# Revit family: ewf_ewg_ewh_ewj-20_105a_b_y_sa2_ta(40a)2-(-50)_50Hz
name_source: partatom
category: 機械設備
units: mm (PartAtom-declared; Revit-internal decimal feet)

## family parameters
OmniClass タイトル = Industrial Ventilating Equipment
OmniClass 番号 = 23.75.35.21.17
パーツ タイプ = 標準
ロード時にボイドで切り取り = はい
丸型コネクタ寸法 = 直径を使用
作業面ベース = いいえ
共有 = いいえ
常に垂直 = はい
部屋計算ポイント = はい

## types (71) — shared parameters
IfcExportAs = IfcFanType
IfcExportType = TUBEAXIAL
MID風量 = 0.0 m³/h
MIN風量 = 0.0 m³/h
OmniClassCode = 23-33 31 19 11 17
URL = https://www.mitsubishielectric.co.jp
Uniclass2015Code = Pr_65_67_29_67
Uniclass2015Title = Propeller fans
Uniclass2015Version = Systems v1.9
ファンの種類 = 軸流羽根
仕様書バージョン = Version1.0
企業コード = 108420
分類コード = 50052503100110
周波数 = 50 Hz
呼称 = 有圧扇
法定耐用年数 = 15
製品リリース年月 = 2022年6月
製品出荷対象 = 国内
製造元 = 三菱電機株式会社
設置方法 = 壁付
説明 = 産業用有圧換気扇 低騒音形 給気専用
負荷分類 = 3_ファン類
運転質量 = 0.00 kg

## per-type parameters (varying)
- EWF-20YSA2-Q: Depth=197; Height=320; MAX風量=660.0 m³/h; Width=320; オリフィス_Depth=100  [stored 0.328084 ft]; オリフィス径=233  [stored 0.764436 ft]; フレームの厚さ=10  [stored 0.0328084 ft]; モデル=EWF-20YSA2-Q; モーター径=5  [stored 0.0164042 ft]; モーター表示=いいえ; レグ_Depth=182  [stored 0.597113 ft]; レグ_Height=230  [stored 0.754593 ft]; レグ_Width=230  [stored 0.754593 ft]; 価格=45400 $; 極=4; 極数=2; 消費電力=30 W; 相=1; 羽根径=∅200; 製品質量=3.30 kg; 質量=3.96 kg; 銘板_H=52; 銘板_Height=136; 銘板_Width=103; 銘板表示=はい; 電動機出力=15 W; 電圧=100 V
- EWF-25ASA2-Q: Depth=201  [stored 0.659449 ft]; Height=370; MAX風量=1140.0 m³/h; Width=370; オリフィス_Depth=110  [stored 0.360892 ft]; オリフィス径=283; フレームの厚さ=10  [stored 0.0328084 ft]; モデル=EWF-25ASA2-Q; モーター径=5  [stored 0.0164042 ft]; モーター表示=いいえ; レグ_Depth=182  [stored 0.597113 ft]; レグ_Height=280; レグ_Width=280; 価格=48100 $; 極=4; 極数=2; 消費電力=42 W; 相=1; 羽根径=∅250; 製品質量=4.30 kg; 質量=5.16 kg; 銘板_H=60  [stored 0.19685 ft]; 銘板_Height=153  [stored 0.501969 ft]; 銘板_Width=120  [stored 0.393701 ft]; 銘板表示=はい; 電動機出力=25 W; 電圧=100 V
- EWF-30BSA2-Q: Depth=197; Height=420; MAX風量=1680.0 m³/h; Width=420; オリフィス_Depth=110  [stored 0.360892 ft]; オリフィス径=323; フレームの厚さ=10  [stored 0.0328084 ft]; モデル=EWF-30BSA2-Q; モーター径=5  [stored 0.0164042 ft]; モーター表示=いいえ; レグ_Depth=179  [stored 0.58727 ft]; レグ_Height=330; レグ_Width=330; 価格=62000 $; 極=4; 極数=2; 消費電力=73 W; 相=1; 羽根径=∅300; 製品質量=5.80 kg; 質量=6.96 kg; 銘板_H=60  [stored 0.19685 ft]; 銘板_Height=153  [stored 0.501969 ft]; 銘板_Width=120  [stored 0.393701 ft]; 銘板表示=はい; 電動機出力=50 W; 電圧=100 V
- EWF-35CSA2-Q: Depth=208; Height=470; MAX風量=2400.0 m³/h; Width=470; オリフィス_Depth=130  [stored 0.426509 ft]; オリフィス径=373; フレームの厚さ=10  [stored 0.0328084 ft]; モデル=EWF-35CSA2-Q; モーター径=5  [stored 0.0164042 ft]; モーター表示=いいえ; レグ_Depth=190; レグ_Height=385; レグ_Width=385; 価格=82500 $; 極=4; 極数=2; 消費電力=91 W; 相=1; 羽根径=∅350; 製品質量=6.60 kg; 質量=7.92 kg; 銘板_H=60  [stored 0.19685 ft]; 銘板_Height=153  [stored 0.501969 ft]; 銘板_Width=120  [stored 0.393701 ft]; 銘板表示=はい; 電動機出力=100 W; 電圧=100 V
- EWF-35DSA2-Q: Depth=259; Height=470; MAX風量=3000.0 m³/h; Width=470; オリフィス_Depth=130  [stored 0.426509 ft]; オリフィス径=373; フレームの厚さ=10  [stored 0.0328084 ft]; モデル=EWF-35DSA2-Q; モーター径=5  [stored 0.0164042 ft]; モーター表示=いいえ; レグ_Depth=227; レグ_Height=385; レグ_Width=385; 価格=90800 $; 極=4; 極数=2; 消費電力=129 W; 相=1; 羽根径=∅350; 製品質量=9.50 kg; 質量=11.40 kg; 銘板_H=73  [stored 0.239501 ft]; 銘板_Height=181  [stored 0.593832 ft]; 銘板_Width=148  [stored 0.485564 ft]; 銘板表示=はい; 電動機出力=150 W; 電圧=100 V
- EWF-40DSA2-Q: Depth=266; Height=520; MAX風量=3720.0 m³/h; Width=520; オリフィス_Depth=135  [stored 0.442913 ft]; オリフィス径=423; フレームの厚さ=10  [stored 0.0328084 ft]; モデル=EWF-40DSA2-Q; モーター径=5  [stored 0.0164042 ft]; モーター表示=いいえ; レグ_Depth=237; レグ_Height=413; レグ_Width=413; 価格=107000 $; 極=4; 極数=2; 消費電力=152 W; 相=1; 羽根径=∅400; 製品質量=12.10 kg; 質量=14.52 kg; 銘板_H=73  [stored 0.239501 ft]; 銘板_Height=181  [stored 0.593832 ft]; 銘板_Width=148  [stored 0.485564 ft]; 銘板表示=はい; 電動機出力=200 W; 電圧=100 V
- EWG-40BSA2-Q: Depth=223  [stored 0.731627 ft]; Height=520; MAX風量=2340.0 m³/h; Width=520; オリフィス_Depth=135  [stored 0.442913 ft]; オリフィス径=423; フレームの厚さ=10  [stored 0.0328084 ft]; モデル=EWG-40BSA2-Q; モーター径=5  [stored 0.0164042 ft]; モーター表示=いいえ; レグ_Depth=207  [stored 0.679134 ft]; レグ_Height=413; レグ_Width=413; 価格=89400 $; 極=6; 極数=2; 消費電力=62 W; 相=1; 羽根径=∅400; 製品質量=8.40 kg; 質量=10.08 kg; 銘板_H=60  [stored 0.19685 ft]; 銘板_Height=153  [stored 0.501969 ft]; 銘板_Width=120  [stored 0.393701 ft]; 銘板表示=はい; 電動機出力=50 W; 電圧=100 V
- EWG-40CSA2-Q: Depth=285; Height=520; MAX風量=3180.0 m³/h; Width=520; オリフィス_Depth=135  [stored 0.442913 ft]; オリフィス径=423; フレームの厚さ=10  [stored 0.0328084 ft]; モデル=EWG-40CSA2-Q; モーター径=5  [stored 0.0164042 ft]; モーター表示=いいえ; レグ_Depth=256; レグ_Height=413; レグ_Width=413; 価格=105000 $; 極=6; 極数=2; 消費電力=112 W; 相=1; 羽根径=∅400; 製品質量=12.20 kg; 質量=14.64 kg; 銘板_H=73  [stored 0.239501 ft]; 銘板_Height=181  [stored 0.593832 ft]; 銘板_Width=148  [stored 0.485564 ft]; 銘板表示=はい; 電動機出力=100 W; 電圧=100 V
- EWF-45ESA2-Q: Depth=307; Height=620; MAX風量=5560.0 m³/h; Width=620; オリフィス_Depth=135  [stored 0.442913 ft]; オリフィス径=473; フレームの厚さ=10  [stored 0.0328084 ft]; モデル=EWF-45ESA2-Q; モーター径=5  [stored 0.0164042 ft]; モーター表示=いいえ; レグ_Depth=274; レグ_Height=522; レグ_Width=522; 価格=135000 $; 極=4; 極数=2; 消費電力=262 W; 相=1; 羽根径=∅450; 製品質量=18.30 kg; 質量=21.96 kg; 銘板_H=88  [stored 0.288714 ft]; 銘板_Height=211  [stored 0.692257 ft]; 銘板_Width=178  [stored 0.58399 ft]; 銘板表示=はい; 電動機出力=400 W; 電圧=100 V
- EWG-45DSA2-Q: Depth=335; Height=620; MAX風量=4200.0 m³/h; Width=620; オリフィス_Depth=135  [stored 0.442913 ft]; オリフィス径=473; フレームの厚さ=10  [stored 0.0328084 ft]; モデル=EWG-45DSA2-Q; モーター径=5  [stored 0.0164042 ft]; モーター表示=いいえ; レグ_Depth=302; レグ_Height=514; レグ_Width=514; 価格=123000 $; 極=6; 極数=2; 消費電力=175 W; 相=1; 羽根径=∅450; 製品質量=16.90 kg; 質量=20.28 kg; 銘板_H=88  [stored 0.288714 ft]; 銘板_Height=211  [stored 0.692257 ft]; 銘板_Width=178  [stored 0.58399 ft]; 銘板表示=はい; 電動機出力=200 W; 電圧=100 V
- EWF-25ATA2-Q_200V: Depth=211  [stored 0.692257 ft]; Height=370; MAX風量=1140.0 m³/h; Width=370; オリフィス_Depth=110  [stored 0.360892 ft]; オリフィス径=283; フレームの厚さ=10  [stored 0.0328084 ft]; モデル=EWF-25ATA2-Q; モーター径=5  [stored 0.0164042 ft]; モーター表示=いいえ; レグ_Depth=197; レグ_Height=280; レグ_Width=280; 価格=48100 $; 極=4; 極数=3; 消費電力=35 W; 相=3; 羽根径=∅250; 製品質量=4.90 kg; 質量=5.88 kg; 銘板_H=60  [stored 0.19685 ft]; 銘板_Height=153  [stored 0.501969 ft]; 銘板_Width=120  [stored 0.393701 ft]; 銘板表示=はい; 電動機出力=25 W; 電圧=200 V
- EWF-30BTA2-Q_200V: Depth=197; Height=420; MAX風量=1680.0 m³/h; Width=420; オリフィス_Depth=110  [stored 0.360892 ft]; オリフィス径=323; フレームの厚さ=10  [stored 0.0328084 ft]; モデル=EWF-30BTA2-Q; モーター径=5  [stored 0.0164042 ft]; モーター表示=いいえ; レグ_Depth=179  [stored 0.58727 ft]; レグ_Height=330; レグ_Width=330; 価格=62000 $; 極=4; 極数=3; 消費電力=57 W; 相=3; 羽根径=∅300; 製品質量=5.80 kg; 質量=6.96 kg; 銘板_H=60  [stored 0.19685 ft]; 銘板_Height=153  [stored 0.501969 ft]; 銘板_Width=120  [stored 0.393701 ft]; 銘板表示=はい; 電動機出力=50 W; 電圧=200 V
- EWF-35CTA2-Q_200V: Depth=208; Height=470; MAX風量=2400.0 m³/h; Width=470; オリフィス_Depth=130  [stored 0.426509 ft]; オリフィス径=373; フレームの厚さ=10  [stored 0.0328084 ft]; モデル=EWF-35CTA2-Q; モーター径=5  [stored 0.0164042 ft]; モーター表示=いいえ; レグ_Depth=190; レグ_Height=385; レグ_Width=385; 価格=82500 $; 極=4; 極数=3; 消費電力=82 W; 相=3; 羽根径=∅350; 製品質量=6.70 kg; 質量=8.04 kg; 銘板_H=60  [stored 0.19685 ft]; 銘板_Height=153  [stored 0.501969 ft]; 銘板_Width=120  [stored 0.393701 ft]; 銘板表示=はい; 電動機出力=100 W; 電圧=200 V
- EWF-35DTA2-Q_200V: Depth=259; Height=470; MAX風量=3000.0 m³/h; Width=470; オリフィス_Depth=130  [stored 0.426509 ft]; オリフィス径=373; フレームの厚さ=10  [stored 0.0328084 ft]; モデル=EWF-35DTA2-Q; モーター径=5  [stored 0.0164042 ft]; モーター表示=いいえ; レグ_Depth=227; レグ_Height=385; レグ_Width=385; 価格=90800 $; 極=4; 極数=3; 消費電力=120 W; 相=3; 羽根径=∅350; 製品質量=9.50 kg; 質量=11.40 kg; 銘板_H=73  [stored 0.239501 ft]; 銘板_Height=181  [stored 0.593832 ft]; 銘板_Width=148  [stored 0.485564 ft]; 銘板表示=はい; 電動機出力=150 W; 電圧=200 V
- EWF-40DTA2-Q_200V: Depth=266; Height=520; MAX風量=3720.0 m³/h; Width=520; オリフィス_Depth=135  [stored 0.442913 ft]; オリフィス径=423; フレームの厚さ=10  [stored 0.0328084 ft]; モデル=EWF-40DTA2-Q; モーター径=5  [stored 0.0164042 ft]; モーター表示=いいえ; レグ_Depth=237; レグ_Height=413; レグ_Width=413; 価格=107000 $; 極=4; 極数=3; 消費電力=147 W; 相=3; 羽根径=∅400; 製品質量=12.20 kg; 質量=14.64 kg; 銘板_H=73  [stored 0.239501 ft]; 銘板_Height=181  [stored 0.593832 ft]; 銘板_Width=148  [stored 0.485564 ft]; 銘板表示=はい; 電動機出力=200 W; 電圧=200 V
- EWF-40ETA2-Q_200V: Depth=308; Height=520; MAX風量=4800.0 m³/h; Width=520; オリフィス_Depth=135  [stored 0.442913 ft]; オリフィス径=423; フレームの厚さ=10  [stored 0.0328084 ft]; モデル=EWF-40ETA2-Q; モーター径=131  [stored 0.42979 ft]; モーター表示=はい; レグ_Depth=279; レグ_Height=414; レグ_Width=414; 価格=117000 $; 極=4; 極数=3; 消費電力=244 W; 相=3; 羽根径=∅400; 製品質量=14.20 kg; 質量=17.04 kg; 銘板_H=5  [stored 0.0164042 ft]; 銘板_Height=5  [stored 0.0164042 ft]; 銘板_Width=5  [stored 0.0164042 ft]; 銘板表示=いいえ; 電動機出力=400 W; 電圧=200 V
- EWG-40BTA2-Q_200V: Depth=223  [stored 0.731627 ft]; Height=520; MAX風量=2340.0 m³/h; Width=520; オリフィス_Depth=135  [stored 0.442913 ft]; オリフィス径=423; フレームの厚さ=10  [stored 0.0328084 ft]; モデル=EWG-40BTA2-Q; モーター径=5  [stored 0.0164042 ft]; モーター表示=いいえ; レグ_Depth=207  [stored 0.679134 ft]; レグ_Height=413; レグ_Width=413; 価格=89400 $; 極=6; 極数=3; 消費電力=57 W; 相=3; 羽根径=∅400; 製品質量=8.30 kg; 質量=9.96 kg; 銘板_H=60  [stored 0.19685 ft]; 銘板_Height=153  [stored 0.501969 ft]; 銘板_Width=120  [stored 0.393701 ft]; 銘板表示=はい; 電動機出力=50 W; 電圧=200 V
- EWG-40CTA2-Q_200V: Depth=308; Height=520; MAX風量=3180.0 m³/h; Width=520; オリフィス_Depth=135  [stored 0.442913 ft]; オリフィス径=423; フレームの厚さ=10  [stored 0.0328084 ft]; モデル=EWG-40CTA2-Q; モーター径=131  [stored 0.42979 ft]; モーター表示=はい; レグ_Depth=251; レグ_Height=413; レグ_Width=413; 価格=105000 $; 極=6; 極数=3; 消費電力=106 W; 相=3; 羽根径=∅400; 製品質量=12.10 kg; 質量=14.52 kg; 銘板_H=5  [stored 0.0164042 ft]; 銘板_Height=5  [stored 0.0164042 ft]; 銘板_Width=5  [stored 0.0164042 ft]; 銘板表示=いいえ; 電動機出力=100 W; 電圧=200 V
- EWF-45ETA2-Q_200V: Depth=315; Height=620; MAX風量=5700.0 m³/h; Width=620; オリフィス_Depth=135  [stored 0.442913 ft]; オリフィス径=473; フレームの厚さ=10  [stored 0.0328084 ft]; モデル=EWF-45ETA2-Q; モーター径=131  [stored 0.42979 ft]; モーター表示=はい; レグ_Depth=286; レグ_Height=522; レグ_Width=522; 価格=135000 $; 極=4; 極数=3; 消費電力=245 W; 相=3; 羽根径=∅450; 製品質量=17.80 kg; 質量=21.36 kg; 銘板_H=5  [stored 0.0164042 ft]; 銘板_Height=5  [stored 0.0164042 ft]; 銘板_Width=5  [stored 0.0164042 ft]; 銘板表示=いいえ; 電動機出力=400 W; 電圧=200 V
- EWG-45DTA2-Q_200V: Depth=315; Height=620; MAX風量=4360.0 m³/h; Width=620; オリフィス_Depth=135  [stored 0.442913 ft]; オリフィス径=473; フレームの厚さ=10  [stored 0.0328084 ft]; モデル=EWG-45DTA2-Q; モーター径=131  [stored 0.42979 ft]; モーター表示=はい; レグ_Depth=286; レグ_Height=522; レグ_Width=522; 価格=123000 $; 極=6; 極数=3; 消費電力=155 W; 相=3; 羽根径=∅450; 製品質量=15.70 kg; 質量=18.84 kg; 銘板_H=5  [stored 0.0164042 ft]; 銘板_Height=5  [stored 0.0164042 ft]; 銘板_Width=5  [stored 0.0164042 ft]; 銘板表示=いいえ; 電動機出力=200 W; 電圧=200 V
- EWF-25ATA2-Q_220V: Depth=211  [stored 0.692257 ft]; Height=370; MAX風量=1140.0 m³/h; Width=370; オリフィス_Depth=110  [stored 0.360892 ft]; オリフィス径=283; フレームの厚さ=10  [stored 0.0328084 ft]; モデル=EWF-25ATA2-Q; モーター径=5  [stored 0.0164042 ft]; モーター表示=いいえ; レグ_Depth=197; レグ_Height=280; レグ_Width=280; 価格=48100 $; 極=4; 極数=3; 消費電力=36 W; 相=3; 羽根径=∅250; 製品質量=4.90 kg; 質量=5.88 kg; 銘板_H=60  [stored 0.19685 ft]; 銘板_Height=153  [stored 0.501969 ft]; 銘板_Width=120  [stored 0.393701 ft]; 銘板表示=はい; 電動機出力=25 W; 電圧=220 V
- EWF-30BTA2-Q_220V: Depth=197; Height=420; MAX風量=1680.0 m³/h; Width=420; オリフィス_Depth=110  [stored 0.360892 ft]; オリフィス径=323; フレームの厚さ=10  [stored 0.0328084 ft]; モデル=EWF-30BTA2-Q; モーター径=5  [stored 0.0164042 ft]; モーター表示=いいえ; レグ_Depth=179  [stored 0.58727 ft]; レグ_Height=330; レグ_Width=330; 価格=62000 $; 極=4; 極数=3; 消費電力=67 W; 相=3; 羽根径=∅300; 製品質量=5.80 kg; 質量=6.96 kg; 銘板_H=60  [stored 0.19685 ft]; 銘板_Height=153  [stored 0.501969 ft]; 銘板_Width=120  [stored 0.393701 ft]; 銘板表示=はい; 電動機出力=50 W; 電圧=220 V
- EWF-35CTA2-Q_220V: Depth=208; Height=470; MAX風量=2400.0 m³/h; Width=470; オリフィス_Depth=130  [stored 0.426509 ft]; オリフィス径=373; フレームの厚さ=10  [stored 0.0328084 ft]; モデル=EWF-35CTA2-Q; モーター径=5  [stored 0.0164042 ft]; モーター表示=いいえ; レグ_Depth=190; レグ_Height=385; レグ_Width=385; 価格=82500 $; 極=4; 極数=3; 消費電力=95 W; 相=3; 羽根径=∅350; 製品質量=6.70 kg; 質量=8.04 kg; 銘板_H=60  [stored 0.19685 ft]; 銘板_Height=153  [stored 0.501969 ft]; 銘板_Width=120  [stored 0.393701 ft]; 銘板表示=はい; 電動機出力=100 W; 電圧=220 V
- EWF-35DTA2-Q_220V: Depth=259; Height=470; MAX風量=3000.0 m³/h; Width=470; オリフィス_Depth=130  [stored 0.426509 ft]; オリフィス径=373; フレームの厚さ=10  [stored 0.0328084 ft]; モデル=EWF-35DTA2-Q; モーター径=5  [stored 0.0164042 ft]; モーター表示=いいえ; レグ_Depth=227; レグ_Height=385; レグ_Width=385; 価格=90800 $; 極=4; 極数=3; 消費電力=132 W; 相=3; 羽根径=∅350; 製品質量=9.50 kg; 質量=11.40 kg; 銘板_H=73  [stored 0.239501 ft]; 銘板_Height=181  [stored 0.593832 ft]; 銘板_Width=148  [stored 0.485564 ft]; 銘板表示=はい; 電動機出力=150 W; 電圧=220 V
- EWF-40DTA2-Q_220V: Depth=266; Height=520; MAX風量=3720.0 m³/h; Width=520; オリフィス_Depth=135  [stored 0.442913 ft]; オリフィス径=423; フレームの厚さ=10  [stored 0.0328084 ft]; モデル=EWF-40DTA2-Q; モーター径=5  [stored 0.0164042 ft]; モーター表示=いいえ; レグ_Depth=237; レグ_Height=413; レグ_Width=413; 価格=107000 $; 極=4; 極数=3; 消費電力=161 W; 相=3; 羽根径=∅400; 製品質量=12.20 kg; 質量=14.64 kg; 銘板_H=73  [stored 0.239501 ft]; 銘板_Height=181  [stored 0.593832 ft]; 銘板_Width=148  [stored 0.485564 ft]; 銘板表示=はい; 電動機出力=200 W; 電圧=220 V
- EWF-40ETA2-Q_220V: Depth=308; Height=520; MAX風量=4800.0 m³/h; Width=520; オリフィス_Depth=135  [stored 0.442913 ft]; オリフィス径=423; フレームの厚さ=10  [stored 0.0328084 ft]; モデル=EWF-40ETA2-Q; モーター径=131  [stored 0.42979 ft]; モーター表示=はい; レグ_Depth=279; レグ_Height=414; レグ_Width=414; 価格=117000 $; 極=4; 極数=3; 消費電力=260 W; 相=3; 羽根径=∅400; 製品質量=14.20 kg; 質量=17.04 kg; 銘板_H=5  [stored 0.0164042 ft]; 銘板_Height=5  [stored 0.0164042 ft]; 銘板_Width=5  [stored 0.0164042 ft]; 銘板表示=いいえ; 電動機出力=400 W; 電圧=220 V
- EWG-40BTA2-Q_220V: Depth=223  [stored 0.731627 ft]; Height=520; MAX風量=2340.0 m³/h; Width=520; オリフィス_Depth=135  [stored 0.442913 ft]; オリフィス径=423; フレームの厚さ=10  [stored 0.0328084 ft]; モデル=EWG-40BTA2-Q; モーター径=5  [stored 0.0164042 ft]; モーター表示=いいえ; レグ_Depth=207  [stored 0.679134 ft]; レグ_Height=413; レグ_Width=413; 価格=89400 $; 極=6; 極数=3; 消費電力=67 W; 相=3; 羽根径=∅400; 製品質量=8.30 kg; 質量=9.96 kg; 銘板_H=60  [stored 0.19685 ft]; 銘板_Height=153  [stored 0.501969 ft]; 銘板_Width=120  [stored 0.393701 ft]; 銘板表示=はい; 電動機出力=50 W; 電圧=220 V
- EWG-40CTA2-Q_220V: Depth=308; Height=520; MAX風量=3180.0 m³/h; Width=520; オリフィス_Depth=135  [stored 0.442913 ft]; オリフィス径=423; フレームの厚さ=10  [stored 0.0328084 ft]; モデル=EWG-40CTA2-Q; モーター径=131  [stored 0.42979 ft]; モーター表示=はい; レグ_Depth=251; レグ_Height=413; レグ_Width=413; 価格=105000 $; 極=6; 極数=3; 消費電力=121 W; 相=3; 羽根径=∅400; 製品質量=12.10 kg; 質量=14.52 kg; 銘板_H=5  [stored 0.0164042 ft]; 銘板_Height=5  [stored 0.0164042 ft]; 銘板_Width=5  [stored 0.0164042 ft]; 銘板表示=いいえ; 電動機出力=100 W; 電圧=220 V
- EWF-45ETA2-Q_220V: Depth=315; Height=620; MAX風量=5700.0 m³/h; Width=620; オリフィス_Depth=135  [stored 0.442913 ft]; オリフィス径=473; フレームの厚さ=10  [stored 0.0328084 ft]; モデル=EWF-45ETA2-Q; モーター径=131  [stored 0.42979 ft]; モーター表示=はい; レグ_Depth=286; レグ_Height=522; レグ_Width=522; 価格=135000 $; 極=4; 極数=3; 消費電力=255 W; 相=3; 羽根径=∅450; 製品質量=17.80 kg; 質量=21.36 kg; 銘板_H=5  [stored 0.0164042 ft]; 銘板_Height=5  [stored 0.0164042 ft]; 銘板_Width=5  [stored 0.0164042 ft]; 銘板表示=いいえ; 電動機出力=400 W; 電圧=220 V
- EWG-45DTA2-Q_220V: Depth=315; Height=620; MAX風量=4360.0 m³/h; Width=620; オリフィス_Depth=135  [stored 0.442913 ft]; オリフィス径=473; フレームの厚さ=10  [stored 0.0328084 ft]; モデル=EWG-45DTA2-Q; モーター径=131  [stored 0.42979 ft]; モーター表示=はい; レグ_Depth=286; レグ_Height=522; レグ_Width=522; 価格=123000 $; 極=6; 極数=3; 消費電力=165 W; 相=3; 羽根径=∅450; 製品質量=15.70 kg; 質量=18.84 kg; 銘板_H=5  [stored 0.0164042 ft]; 銘板_Height=5  [stored 0.0164042 ft]; 銘板_Width=5  [stored 0.0164042 ft]; 銘板表示=いいえ; 電動機出力=200 W; 電圧=220 V
- EWF-50FTA2-Q_200V: Depth=295; Height=620; MAX風量=6900.0 m³/h; Width=620; オリフィス_Depth=155  [stored 0.50853 ft]; オリフィス径=528; フレームの厚さ=10  [stored 0.0328084 ft]; モデル=EWF-50FTA2-Q; モーター径=131  [stored 0.42979 ft]; モーター表示=はい; レグ_Depth=266; レグ_Height=522; レグ_Width=522; 価格=146000 $; 極=4; 極数=3; 消費電力=347 W; 相=3; 羽根径=∅500; 製品質量=19.70 kg; 質量=23.64 kg; 銘板_H=5  [stored 0.0164042 ft]; 銘板_Height=5  [stored 0.0164042 ft]; 銘板_Width=5  [stored 0.0164042 ft]; 銘板表示=いいえ; 電動機出力=750 W; 電圧=200 V
- EWG-50DTA2-Q_200V: Depth=295; Height=620; MAX風量=4800.0 m³/h; Width=620; オリフィス_Depth=155  [stored 0.50853 ft]; オリフィス径=528; フレームの厚さ=10  [stored 0.0328084 ft]; モデル=EWG-50DTA2-Q; モーター径=131  [stored 0.42979 ft]; モーター表示=はい; レグ_Depth=266; レグ_Height=522; レグ_Width=522; 価格=118000 $; 極=6; 極数=3; 消費電力=115 W; 相=3; 羽根径=∅500; 製品質量=15.40 kg; 質量=18.48 kg; 銘板_H=5  [stored 0.0164042 ft]; 銘板_Height=5  [stored 0.0164042 ft]; 銘板_Width=5  [stored 0.0164042 ft]; 銘板表示=いいえ; 電動機出力=200 W; 電圧=200 V
- EWG-50ETA2-Q_200V: Depth=326; Height=620; MAX風量=6060.0 m³/h; Width=620; オリフィス_Depth=155  [stored 0.50853 ft]; オリフィス径=528; フレームの厚さ=10  [stored 0.0328084 ft]; モデル=EWG-50ETA2-Q; モーター径=131  [stored 0.42979 ft]; モーター表示=はい; レグ_Depth=297; レグ_Height=522; レグ_Width=522; 価格=136000 $; 極=6; 極数=3; 消費電力=266 W; 相=3; 羽根径=∅500; 製品質量=18.50 kg; 質量=22.20 kg; 銘板_H=5  [stored 0.0164042 ft]; 銘板_Height=5  [stored 0.0164042 ft]; 銘板_Width=5  [stored 0.0164042 ft]; 銘板表示=いいえ; 電動機出力=400 W; 電圧=200 V
- EWF-60HTA2-Q_200V: Depth=346; Height=710; MAX風量=12500.0 m³/h; Width=710; オリフィス_Depth=175  [stored 0.574147 ft]; オリフィス径=624; フレームの厚さ=10  [stored 0.0328084 ft]; モデル=EWF-60HTA2-Q; モーター径=202  [stored 0.66273 ft]; モーター表示=はい; レグ_Depth=261; レグ_Height=624; レグ_Width=624; 価格=258000 $; 極=4; 極数=3; 消費電力=705 W; 相=3; 羽根径=∅600; 製品質量=28.00 kg; 質量=33.60 kg; 銘板_H=5  [stored 0.0164042 ft]; 銘板_Height=5  [stored 0.0164042 ft]; 銘板_Width=5  [stored 0.0164042 ft]; 銘板表示=いいえ; 電動機出力=2200 W; 電圧=200 V
- EWG-60ETA2-Q_200V: Depth=317; Height=710; MAX風量=7860.0 m³/h; Width=710; オリフィス_Depth=175  [stored 0.574147 ft]; オリフィス径=624; フレームの厚さ=10  [stored 0.0328084 ft]; モデル=EWG-60ETA2-Q; モーター径=131  [stored 0.42979 ft]; モーター表示=はい; レグ_Depth=288; レグ_Height=612; レグ_Width=612; 価格=154000 $; 極=6; 極数=3; 消費電力=235 W; 相=3; 羽根径=∅600; 製品質量=20.30 kg; 質量=24.36 kg; 銘板_H=5  [stored 0.0164042 ft]; 銘板_Height=5  [stored 0.0164042 ft]; 銘板_Width=5  [stored 0.0164042 ft]; 銘板表示=いいえ; 電動機出力=400 W; 電圧=200 V
- EWG-60FTA2-Q_200V: Depth=347; Height=710; MAX風量=9420.0 m³/h; Width=710; オリフィス_Depth=175  [stored 0.574147 ft]; オリフィス径=624; フレームの厚さ=10  [stored 0.0328084 ft]; モデル=EWG-60FTA2-Q; モーター径=163  [stored 0.534777 ft]; モーター表示=はい; レグ_Depth=309; レグ_Height=612; レグ_Width=612; 価格=181000 $; 極=6; 極数=3; 消費電力=406 W; 相=3; 羽根径=∅600; 製品質量=27.10 kg; 質量=32.52 kg; 銘板_H=5  [stored 0.0164042 ft]; 銘板_Height=5  [stored 0.0164042 ft]; 銘板_Width=5  [stored 0.0164042 ft]; 銘板表示=いいえ; 電動機出力=750 W; 電圧=200 V
- EWF-50FTA2-Q_220V: Depth=295; Height=620; MAX風量=6900.0 m³/h; Width=620; オリフィス_Depth=155  [stored 0.50853 ft]; オリフィス径=528; フレームの厚さ=10  [stored 0.0328084 ft]; モデル=EWF-50FTA2-Q; モーター径=131  [stored 0.42979 ft]; モーター表示=はい; レグ_Depth=266; レグ_Height=522; レグ_Width=522; 価格=146000 $; 極=4; 極数=3; 消費電力=368 W; 相=3; 羽根径=∅500; 製品質量=19.70 kg; 質量=23.64 kg; 銘板_H=5  [stored 0.0164042 ft]; 銘板_Height=5  [stored 0.0164042 ft]; 銘板_Width=5  [stored 0.0164042 ft]; 銘板表示=いいえ; 電動機出力=750 W; 電圧=220 V
- EWG-50DTA2-Q_220V: Depth=295; Height=620; MAX風量=4800.0 m³/h; Width=620; オリフィス_Depth=155  [stored 0.50853 ft]; オリフィス径=528; フレームの厚さ=10  [stored 0.0328084 ft]; モデル=EWG-50DTA2-Q; モーター径=131  [stored 0.42979 ft]; モーター表示=はい; レグ_Depth=266; レグ_Height=522; レグ_Width=522; 価格=118000 $; 極=6; 極数=3; 消費電力=125 W; 相=3; 羽根径=∅500; 製品質量=15.40 kg; 質量=18.48 kg; 銘板_H=5  [stored 0.0164042 ft]; 銘板_Height=5  [stored 0.0164042 ft]; 銘板_Width=5  [stored 0.0164042 ft]; 銘板表示=いいえ; 電動機出力=200 W; 電圧=220 V
- EWG-50ETA2-Q_220V: Depth=326; Height=620; MAX風量=6060.0 m³/h; Width=620; オリフィス_Depth=155  [stored 0.50853 ft]; オリフィス径=528; フレームの厚さ=10  [stored 0.0328084 ft]; モデル=EWG-50ETA2-Q; モーター径=131  [stored 0.42979 ft]; モーター表示=はい; レグ_Depth=297; レグ_Height=522; レグ_Width=522; 価格=136000 $; 極=6; 極数=3; 消費電力=295 W; 相=3; 羽根径=∅500; 製品質量=18.50 kg; 質量=22.20 kg; 銘板_H=5  [stored 0.0164042 ft]; 銘板_Height=5  [stored 0.0164042 ft]; 銘板_Width=5  [stored 0.0164042 ft]; 銘板表示=いいえ; 電動機出力=400 W; 電圧=220 V
- EWF-60HTA2-Q_220V: Depth=346; Height=710; MAX風量=12500.0 m³/h; Width=710; オリフィス_Depth=175  [stored 0.574147 ft]; オリフィス径=624; フレームの厚さ=10  [stored 0.0328084 ft]; モデル=EWF-60HTA2-Q; モーター径=202  [stored 0.66273 ft]; モーター表示=はい; レグ_Depth=261; レグ_Height=624; レグ_Width=624; 価格=258000 $; 極=4; 極数=3; 消費電力=770 W; 相=3; 羽根径=∅600; 製品質量=28.00 kg; 質量=33.60 kg; 銘板_H=5  [stored 0.0164042 ft]; 銘板_Height=5  [stored 0.0164042 ft]; 銘板_Width=5  [stored 0.0164042 ft]; 銘板表示=いいえ; 電動機出力=2200 W; 電圧=220 V
- EWG-60ETA2-Q_220V: Depth=317; Height=710; MAX風量=7860.0 m³/h; Width=710; オリフィス_Depth=175  [stored 0.574147 ft]; オリフィス径=624; フレームの厚さ=10  [stored 0.0328084 ft]; モデル=EWG-60ETA2-Q; モーター径=131  [stored 0.42979 ft]; モーター表示=はい; レグ_Depth=288; レグ_Height=612; レグ_Width=612; 価格=154000 $; 極=6; 極数=3; 消費電力=251 W; 相=3; 羽根径=∅600; 製品質量=20.30 kg; 質量=24.36 kg; 銘板_H=5  [stored 0.0164042 ft]; 銘板_Height=5  [stored 0.0164042 ft]; 銘板_Width=5  [stored 0.0164042 ft]; 銘板表示=いいえ; 電動機出力=400 W; 電圧=220 V
- EWG-60FTA2-Q_220V: Depth=347; Height=710; MAX風量=9420.0 m³/h; Width=710; オリフィス_Depth=175  [stored 0.574147 ft]; オリフィス径=624; フレームの厚さ=10  [stored 0.0328084 ft]; モデル=EWG-60FTA2-Q; モーター径=163  [stored 0.534777 ft]; モーター表示=はい; レグ_Depth=309; レグ_Height=612; レグ_Width=612; 価格=181000 $; 極=6; 極数=3; 消費電力=419 W; 相=3; 羽根径=∅600; 製品質量=27.10 kg; 質量=32.52 kg; 銘板_H=5  [stored 0.0164042 ft]; 銘板_Height=5  [stored 0.0164042 ft]; 銘板_Width=5  [stored 0.0164042 ft]; 銘板表示=いいえ; 電動機出力=750 W; 電圧=220 V
- EWG-70JTA2-Q-50: Depth=465; Height=860; MAX風量=19500.0 m³/h; Width=860; オリフィス_Depth=245; オリフィス径=797; フレームの厚さ=35; モデル=EWG-70JTA2-Q-50; モーター径=289; モーター表示=はい; レグ_Depth=364; レグ_Height=725; レグ_Width=725; 価格=498000 $; 極=6; 極数=3; 消費電力=1160 W; 相=3; 羽根径=∅700; 製品質量=59.00 kg; 質量=70.80 kg; 銘板_H=5  [stored 0.0164042 ft]; 銘板_Height=5  [stored 0.0164042 ft]; 銘板_Width=5  [stored 0.0164042 ft]; 銘板表示=いいえ; 電動機出力=3700 W; 電圧=200 V
- EWG-80LTA2-Q-50: Depth=519; Height=950; MAX風量=27000.0 m³/h; Width=950; オリフィス_Depth=256; オリフィス径=876; フレームの厚さ=35; モデル=EWG-80LTA2-Q-50; モーター径=289; モーター表示=はい; レグ_Depth=405; レグ_Height=786; レグ_Width=786; 価格=731000 $; 極=6; 極数=3; 消費電力=1960 W; 相=3; 羽根径=∅800; 製品質量=76.00 kg; 質量=91.20 kg; 銘板_H=5  [stored 0.0164042 ft]; 銘板_Height=5  [stored 0.0164042 ft]; 銘板_Width=5  [stored 0.0164042 ft]; 銘板表示=いいえ; 電動機出力=7500 W; 電圧=200 V
- EWH-80JTA2-Q-50: Depth=519; Height=950; MAX風量=20000.0 m³/h; Width=950; オリフィス_Depth=256; オリフィス径=876; フレームの厚さ=35; モデル=EWH-80JTA2-Q-50; モーター径=231; モーター表示=はい; レグ_Depth=405; レグ_Height=780; レグ_Width=780; 価格=655000 $; 極=8; 極数=3; 消費電力=895 W; 相=3; 羽根径=∅800; 製品質量=75.00 kg; 質量=90.00 kg; 銘板_H=5  [stored 0.0164042 ft]; 銘板_Height=5  [stored 0.0164042 ft]; 銘板_Width=5  [stored 0.0164042 ft]; 銘板表示=いいえ; 電動機出力=3700 W; 電圧=200 V
- EWH-105MTA2-Q-50: Depth=629; Height=1280; MAX風量=43000.0 m³/h; Width=1280; オリフィス_Depth=303; オリフィス径=1090; フレームの厚さ=50  [stored 0.164042 ft]; モデル=EWH-105MTA2-Q-50; モーター径=305; モーター表示=はい; レグ_Depth=488; レグ_Height=1107; レグ_Width=1107; 価格=1181000 $; 極=8; 極数=3; 消費電力=2700 W; 相=3; 羽根径=∅1050; 製品質量=138.00 kg; 質量=165.60 kg; 銘板_H=5  [stored 0.0164042 ft]; 銘板_Height=5  [stored 0.0164042 ft]; 銘板_Width=5  [stored 0.0164042 ft]; 銘板表示=いいえ; 電動機出力=11000 W; 電圧=200 V
- EWJ-105JTA2-Q-50: Depth=629; Height=1280; MAX風量=34500.0 m³/h; Width=1280; オリフィス_Depth=303; オリフィス径=1090; フレームの厚さ=50  [stored 0.164042 ft]; モデル=EWJ-105JTA2-Q-50; モーター径=262; モーター表示=はい; レグ_Depth=484; レグ_Height=1096; レグ_Width=1096; 価格=1005000 $; 極=10; 極数=3; 消費電力=1540 W; 相=3; 羽根径=∅1050; 製品質量=134.00 kg; 質量=160.80 kg; 銘板_H=5  [stored 0.0164042 ft]; 銘板_Height=5  [stored 0.0164042 ft]; 銘板_Width=5  [stored 0.0164042 ft]; 銘板表示=いいえ; 電動機出力=3700 W; 電圧=200 V
- EWF-25ATA40A2-Q_380V: Depth=201  [stored 0.659449 ft]; Height=370; MAX風量=1140.0 m³/h; Width=370; オリフィス_Depth=110  [stored 0.360892 ft]; オリフィス径=283; フレームの厚さ=10  [stored 0.0328084 ft]; モデル=EWF-25ATA40A2-Q; モーター径=5  [stored 0.0164042 ft]; モーター表示=いいえ; レグ_Depth=187; レグ_Height=280; レグ_Width=280; 価格=53000 $; 極=4; 極数=3; 消費電力=32 W; 相=3; 羽根径=∅250; 製品質量=4.70 kg; 質量=5.64 kg; 銘板_H=60  [stored 0.19685 ft]; 銘板_Height=153  [stored 0.501969 ft]; 銘板_Width=120  [stored 0.393701 ft]; 銘板表示=はい; 電動機出力=25 W; 電圧=380 V
- EWF-30BTA40A2-Q_380V: Depth=197; Height=420; MAX風量=1680.0 m³/h; Width=420; オリフィス_Depth=110  [stored 0.360892 ft]; オリフィス径=323; フレームの厚さ=10  [stored 0.0328084 ft]; モデル=EWF-30BTA40A2-Q; モーター径=5  [stored 0.0164042 ft]; モーター表示=いいえ; レグ_Depth=179  [stored 0.58727 ft]; レグ_Height=330; レグ_Width=330; 価格=68100 $; 極=4; 極数=3; 消費電力=57 W; 相=3; 羽根径=∅300; 製品質量=5.80 kg; 質量=6.96 kg; 銘板_H=60  [stored 0.19685 ft]; 銘板_Height=153  [stored 0.501969 ft]; 銘板_Width=120  [stored 0.393701 ft]; 銘板表示=はい; 電動機出力=50 W; 電圧=380 V
- EWF-35CTA40A2-Q_380V: Depth=208; Height=470; MAX風量=2400.0 m³/h; Width=470; オリフィス_Depth=130  [stored 0.426509 ft]; オリフィス径=373; フレームの厚さ=10  [stored 0.0328084 ft]; モデル=EWF-35CTA40A2-Q; モーター径=5  [stored 0.0164042 ft]; モーター表示=いいえ; レグ_Depth=190; レグ_Height=385; レグ_Width=385; 価格=90800 $; 極=4; 極数=3; 消費電力=80 W; 相=3; 羽根径=∅350; 製品質量=6.70 kg; 質量=8.04 kg; 銘板_H=60  [stored 0.19685 ft]; 銘板_Height=153  [stored 0.501969 ft]; 銘板_Width=120  [stored 0.393701 ft]; 銘板表示=はい; 電動機出力=100 W; 電圧=380 V
- EWF-35DTA40A2-Q_380V: Depth=259; Height=470; MAX風量=3000.0 m³/h; Width=470; オリフィス_Depth=130  [stored 0.426509 ft]; オリフィス径=373; フレームの厚さ=10  [stored 0.0328084 ft]; モデル=EWF-35DTA40A2-Q; モーター径=5  [stored 0.0164042 ft]; モーター表示=いいえ; レグ_Depth=227; レグ_Height=385; レグ_Width=385; 価格=100000 $; 極=4; 極数=3; 消費電力=120 W; 相=3; 羽根径=∅350; 製品質量=9.50 kg; 質量=11.40 kg; 銘板_H=73  [stored 0.239501 ft]; 銘板_Height=181  [stored 0.593832 ft]; 銘板_Width=148  [stored 0.485564 ft]; 銘板表示=はい; 電動機出力=150 W; 電圧=380 V
- EWF-40DTA40A2-Q_380V: Depth=266; Height=520; MAX風量=3720.0 m³/h; Width=520; オリフィス_Depth=135  [stored 0.442913 ft]; オリフィス径=423; フレームの厚さ=10  [stored 0.0328084 ft]; モデル=EWF-40DTA40A2-Q; モーター径=5  [stored 0.0164042 ft]; モーター表示=いいえ; レグ_Depth=237; レグ_Height=413; レグ_Width=413; 価格=115000 $; 極=4; 極数=3; 消費電力=135 W; 相=3; 羽根径=∅400; 製品質量=12.20 kg; 質量=14.64 kg; 銘板_H=73  [stored 0.239501 ft]; 銘板_Height=181  [stored 0.593832 ft]; 銘板_Width=148  [stored 0.485564 ft]; 銘板表示=はい; 電動機出力=200 W; 電圧=380 V
- EWF-40ETA40A2-Q_380V: Depth=308; Height=520; MAX風量=4800.0 m³/h; Width=520; オリフィス_Depth=135  [stored 0.442913 ft]; オリフィス径=423; フレームの厚さ=10  [stored 0.0328084 ft]; モデル=EWF-40ETA40A2-Q; モーター径=131  [stored 0.42979 ft]; モーター表示=はい; レグ_Depth=279; レグ_Height=414; レグ_Width=414; 価格=129000 $; 極=4; 極数=3; 消費電力=235 W; 相=3; 羽根径=∅400; 製品質量=14.20 kg; 質量=17.04 kg; 銘板_H=5  [stored 0.0164042 ft]; 銘板_Height=5  [stored 0.0164042 ft]; 銘板_Width=5  [stored 0.0164042 ft]; 銘板表示=いいえ; 電動機出力=400 W; 電圧=380 V
- EWF-50FTA40A2-Q_380V: Depth=295; Height=620; MAX風量=6900.0 m³/h; Width=620; オリフィス_Depth=155  [stored 0.50853 ft]; オリフィス径=528; フレームの厚さ=10  [stored 0.0328084 ft]; モデル=EWF-50FTA40A2-Q; モーター径=131  [stored 0.42979 ft]; モーター表示=はい; レグ_Depth=266; レグ_Height=522; レグ_Width=522; 価格=163000 $; 極=4; 極数=3; 消費電力=320 W; 相=3; 羽根径=∅500; 製品質量=19.70 kg; 質量=23.64 kg; 銘板_H=5  [stored 0.0164042 ft]; 銘板_Height=5  [stored 0.0164042 ft]; 銘板_Width=5  [stored 0.0164042 ft]; 銘板表示=いいえ; 電動機出力=750 W; 電圧=380 V
- EWG-60FTA40A2-Q_380V: Depth=347; Height=710; MAX風量=9420.0 m³/h; Width=710; オリフィス_Depth=175  [stored 0.574147 ft]; オリフィス径=624; フレームの厚さ=10  [stored 0.0328084 ft]; モデル=EWG-60FTA40A2-Q; モーター径=163  [stored 0.534777 ft]; モーター表示=はい; レグ_Depth=309; レグ_Height=612; レグ_Width=612; 価格=200000 $; 極=6; 極数=3; 消費電力=400 W; 相=3; 羽根径=∅600; 製品質量=27.10 kg; 質量=32.52 kg; 銘板_H=5  [stored 0.0164042 ft]; 銘板_Height=5  [stored 0.0164042 ft]; 銘板_Width=5  [stored 0.0164042 ft]; 銘板表示=いいえ; 電動機出力=750 W; 電圧=380 V
- EWF-25ATA40A2-Q_400V: Depth=201  [stored 0.659449 ft]; Height=370; MAX風量=1140.0 m³/h; Width=370; オリフィス_Depth=110  [stored 0.360892 ft]; オリフィス径=283; フレームの厚さ=10  [stored 0.0328084 ft]; モデル=EWF-25ATA40A2-Q; モーター径=5  [stored 0.0164042 ft]; モーター表示=いいえ; レグ_Depth=187; レグ_Height=280; レグ_Width=280; 価格=53000 $; 極=4; 極数=3; 消費電力=34 W; 相=3; 羽根径=∅250; 製品質量=4.70 kg; 質量=5.64 kg; 銘板_H=60  [stored 0.19685 ft]; 銘板_Height=153  [stored 0.501969 ft]; 銘板_Width=120  [stored 0.393701 ft]; 銘板表示=はい; 電動機出力=25 W; 電圧=400 V
- EWF-30BTA40A2-Q_400V: Depth=197; Height=420; MAX風量=1680.0 m³/h; Width=420; オリフィス_Depth=110  [stored 0.360892 ft]; オリフィス径=323; フレームの厚さ=10  [stored 0.0328084 ft]; モデル=EWF-30BTA40A2-Q; モーター径=5  [stored 0.0164042 ft]; モーター表示=いいえ; レグ_Depth=179  [stored 0.58727 ft]; レグ_Height=330; レグ_Width=330; 価格=68100 $; 極=4; 極数=3; 消費電力=60 W; 相=3; 羽根径=∅300; 製品質量=5.80 kg; 質量=6.96 kg; 銘板_H=60  [stored 0.19685 ft]; 銘板_Height=153  [stored 0.501969 ft]; 銘板_Width=120  [stored 0.393701 ft]; 銘板表示=はい; 電動機出力=50 W; 電圧=400 V
- EWF-35CTA40A2-Q_400V: Depth=208; Height=470; MAX風量=2400.0 m³/h; Width=470; オリフィス_Depth=130  [stored 0.426509 ft]; オリフィス径=373; フレームの厚さ=10  [stored 0.0328084 ft]; モデル=EWF-35CTA40A2-Q; モーター径=5  [stored 0.0164042 ft]; モーター表示=いいえ; レグ_Depth=190; レグ_Height=385; レグ_Width=385; 価格=90800 $; 極=4; 極数=3; 消費電力=86 W; 相=3; 羽根径=∅350; 製品質量=6.70 kg; 質量=8.04 kg; 銘板_H=60  [stored 0.19685 ft]; 銘板_Height=153  [stored 0.501969 ft]; 銘板_Width=120  [stored 0.393701 ft]; 銘板表示=はい; 電動機出力=100 W; 電圧=400 V
- EWF-35DTA40A2-Q_400V: Depth=259; Height=470; MAX風量=3000.0 m³/h; Width=470; オリフィス_Depth=130  [stored 0.426509 ft]; オリフィス径=373; フレームの厚さ=10  [stored 0.0328084 ft]; モデル=EWF-35DTA40A2-Q; モーター径=5  [stored 0.0164042 ft]; モーター表示=いいえ; レグ_Depth=227; レグ_Height=385; レグ_Width=385; 価格=100000 $; 極=4; 極数=3; 消費電力=125 W; 相=3; 羽根径=∅350; 製品質量=9.50 kg; 質量=11.40 kg; 銘板_H=73  [stored 0.239501 ft]; 銘板_Height=181  [stored 0.593832 ft]; 銘板_Width=148  [stored 0.485564 ft]; 銘板表示=はい; 電動機出力=150 W; 電圧=400 V
- EWF-40DTA40A2-Q_400V: Depth=266; Height=520; MAX風量=3720.0 m³/h; Width=520; オリフィス_Depth=135  [stored 0.442913 ft]; オリフィス径=423; フレームの厚さ=10  [stored 0.0328084 ft]; モデル=EWF-40DTA40A2-Q; モーター径=5  [stored 0.0164042 ft]; モーター表示=いいえ; レグ_Depth=237; レグ_Height=413; レグ_Width=413; 価格=115000 $; 極=4; 極数=3; 消費電力=143 W; 相=3; 羽根径=∅400; 製品質量=12.20 kg; 質量=14.64 kg; 銘板_H=73  [stored 0.239501 ft]; 銘板_Height=181  [stored 0.593832 ft]; 銘板_Width=148  [stored 0.485564 ft]; 銘板表示=はい; 電動機出力=200 W; 電圧=400 V
- EWF-40ETA40A2-Q_400V: Depth=308; Height=520; MAX風量=4800.0 m³/h; Width=520; オリフィス_Depth=135  [stored 0.442913 ft]; オリフィス径=423; フレームの厚さ=10  [stored 0.0328084 ft]; モデル=EWF-40ETA40A2-Q; モーター径=131  [stored 0.42979 ft]; モーター表示=はい; レグ_Depth=279; レグ_Height=414; レグ_Width=414; 価格=129000 $; 極=4; 極数=3; 消費電力=235 W; 相=3; 羽根径=∅400; 製品質量=14.20 kg; 質量=17.04 kg; 銘板_H=5  [stored 0.0164042 ft]; 銘板_Height=5  [stored 0.0164042 ft]; 銘板_Width=5  [stored 0.0164042 ft]; 銘板表示=いいえ; 電動機出力=400 W; 電圧=400 V
- EWF-50FTA40A2-Q_400V: Depth=295; Height=620; MAX風量=6900.0 m³/h; Width=620; オリフィス_Depth=155  [stored 0.50853 ft]; オリフィス径=528; フレームの厚さ=10  [stored 0.0328084 ft]; モデル=EWF-50FTA40A2-Q; モーター径=131  [stored 0.42979 ft]; モーター表示=はい; レグ_Depth=266; レグ_Height=522; レグ_Width=522; 価格=163000 $; 極=4; 極数=3; 消費電力=325 W; 相=3; 羽根径=∅500; 製品質量=19.70 kg; 質量=23.64 kg; 銘板_H=5  [stored 0.0164042 ft]; 銘板_Height=5  [stored 0.0164042 ft]; 銘板_Width=5  [stored 0.0164042 ft]; 銘板表示=いいえ; 電動機出力=750 W; 電圧=400 V
- EWG-60FTA40A2-Q_400V: Depth=347; Height=710; MAX風量=9420.0 m³/h; Width=710; オリフィス_Depth=175  [stored 0.574147 ft]; オリフィス径=624; フレームの厚さ=10  [stored 0.0328084 ft]; モデル=EWG-60FTA40A2-Q; モーター径=163  [stored 0.534777 ft]; モーター表示=はい; レグ_Depth=309; レグ_Height=612; レグ_Width=612; 価格=200000 $; 極=6; 極数=3; 消費電力=405 W; 相=3; 羽根径=∅600; 製品質量=27.10 kg; 質量=32.52 kg; 銘板_H=5  [stored 0.0164042 ft]; 銘板_Height=5  [stored 0.0164042 ft]; 銘板_Width=5  [stored 0.0164042 ft]; 銘板表示=いいえ; 電動機出力=750 W; 電圧=400 V
- EWF-25ATA40A2-Q_415V: Depth=201  [stored 0.659449 ft]; Height=370; MAX風量=1140.0 m³/h; Width=370; オリフィス_Depth=110  [stored 0.360892 ft]; オリフィス径=283; フレームの厚さ=10  [stored 0.0328084 ft]; モデル=EWF-25ATA40A2-Q; モーター径=5  [stored 0.0164042 ft]; モーター表示=いいえ; レグ_Depth=187; レグ_Height=280; レグ_Width=280; 価格=53000 $; 極=4; 極数=3; 消費電力=35 W; 相=3; 羽根径=∅250; 製品質量=4.70 kg; 質量=5.64 kg; 銘板_H=60  [stored 0.19685 ft]; 銘板_Height=153  [stored 0.501969 ft]; 銘板_Width=120  [stored 0.393701 ft]; 銘板表示=はい; 電動機出力=25 W; 電圧=415 V
- EWF-30BTA40A2-Q_415V: Depth=197; Height=420; MAX風量=1680.0 m³/h; Width=420; オリフィス_Depth=110  [stored 0.360892 ft]; オリフィス径=323; フレームの厚さ=10  [stored 0.0328084 ft]; モデル=EWF-30BTA40A2-Q; モーター径=5  [stored 0.0164042 ft]; モーター表示=いいえ; レグ_Depth=179  [stored 0.58727 ft]; レグ_Height=330; レグ_Width=330; 価格=68100 $; 極=4; 極数=3; 消費電力=63 W; 相=3; 羽根径=∅300; 製品質量=5.80 kg; 質量=6.96 kg; 銘板_H=60  [stored 0.19685 ft]; 銘板_Height=153  [stored 0.501969 ft]; 銘板_Width=120  [stored 0.393701 ft]; 銘板表示=はい; 電動機出力=50 W; 電圧=415 V
- EWF-35CTA40A2-Q_415V: Depth=208; Height=470; MAX風量=2400.0 m³/h; Width=470; オリフィス_Depth=130  [stored 0.426509 ft]; オリフィス径=373; フレームの厚さ=10  [stored 0.0328084 ft]; モデル=EWF-35CTA40A2-Q; モーター径=5  [stored 0.0164042 ft]; モーター表示=いいえ; レグ_Depth=190; レグ_Height=385; レグ_Width=385; 価格=90800 $; 極=4; 極数=3; 消費電力=90 W; 相=3; 羽根径=∅350; 製品質量=6.70 kg; 質量=8.04 kg; 銘板_H=60  [stored 0.19685 ft]; 銘板_Height=153  [stored 0.501969 ft]; 銘板_Width=120  [stored 0.393701 ft]; 銘板表示=はい; 電動機出力=100 W; 電圧=415 V
- EWF-35DTA40A2-Q_415V: Depth=259; Height=470; MAX風量=3000.0 m³/h; Width=470; オリフィス_Depth=130  [stored 0.426509 ft]; オリフィス径=373; フレームの厚さ=10  [stored 0.0328084 ft]; モデル=EWF-35DTA40A2-Q; モーター径=5  [stored 0.0164042 ft]; モーター表示=いいえ; レグ_Depth=227; レグ_Height=385; レグ_Width=385; 価格=100000 $; 極=4; 極数=3; 消費電力=130 W; 相=3; 羽根径=∅350; 製品質量=9.50 kg; 質量=11.40 kg; 銘板_H=73  [stored 0.239501 ft]; 銘板_Height=181  [stored 0.593832 ft]; 銘板_Width=148  [stored 0.485564 ft]; 銘板表示=はい; 電動機出力=150 W; 電圧=415 V
- EWF-40DTA40A2-Q_415V: Depth=266; Height=520; MAX風量=3720.0 m³/h; Width=520; オリフィス_Depth=135  [stored 0.442913 ft]; オリフィス径=423; フレームの厚さ=10  [stored 0.0328084 ft]; モデル=EWF-40DTA40A2-Q; モーター径=5  [stored 0.0164042 ft]; モーター表示=いいえ; レグ_Depth=237; レグ_Height=413; レグ_Width=413; 価格=115000 $; 極=4; 極数=3; 消費電力=145 W; 相=3; 羽根径=∅400; 製品質量=12.20 kg; 質量=14.64 kg; 銘板_H=73  [stored 0.239501 ft]; 銘板_Height=181  [stored 0.593832 ft]; 銘板_Width=148  [stored 0.485564 ft]; 銘板表示=はい; 電動機出力=200 W; 電圧=415 V
- EWF-40ETA40A2-Q_415V: Depth=308; Height=520; MAX風量=4800.0 m³/h; Width=520; オリフィス_Depth=135  [stored 0.442913 ft]; オリフィス径=423; フレームの厚さ=10  [stored 0.0328084 ft]; モデル=EWF-40ETA40A2-Q; モーター径=131  [stored 0.42979 ft]; モーター表示=はい; レグ_Depth=279; レグ_Height=414; レグ_Width=414; 価格=129000 $; 極=4; 極数=3; 消費電力=235 W; 相=3; 羽根径=∅400; 製品質量=14.20 kg; 質量=17.04 kg; 銘板_H=5  [stored 0.0164042 ft]; 銘板_Height=5  [stored 0.0164042 ft]; 銘板_Width=5  [stored 0.0164042 ft]; 銘板表示=いいえ; 電動機出力=400 W; 電圧=415 V
- EWF-50FTA40A2-Q_415V: Depth=295; Height=620; MAX風量=6900.0 m³/h; Width=620; オリフィス_Depth=155  [stored 0.50853 ft]; オリフィス径=528; フレームの厚さ=10  [stored 0.0328084 ft]; モデル=EWF-50FTA40A2-Q; モーター径=131  [stored 0.42979 ft]; モーター表示=はい; レグ_Depth=266; レグ_Height=522; レグ_Width=522; 価格=163000 $; 極=4; 極数=3; 消費電力=340 W; 相=3; 羽根径=∅500; 製品質量=19.70 kg; 質量=23.64 kg; 銘板_H=5  [stored 0.0164042 ft]; 銘板_Height=5  [stored 0.0164042 ft]; 銘板_Width=5  [stored 0.0164042 ft]; 銘板表示=いいえ; 電動機出力=750 W; 電圧=415 V
- EWG-60FTA40A2-Q_415V: Depth=347; Height=710; MAX風量=9420.0 m³/h; Width=710; オリフィス_Depth=175  [stored 0.574147 ft]; オリフィス径=624; フレームの厚さ=10  [stored 0.0328084 ft]; モデル=EWG-60FTA40A2-Q; モーター径=163  [stored 0.534777 ft]; モーター表示=はい; レグ_Depth=309; レグ_Height=612; レグ_Width=612; 価格=200000 $; 極=6; 極数=3; 消費電力=410 W; 相=3; 羽根径=∅600; 製品質量=27.10 kg; 質量=32.52 kg; 銘板_H=5  [stored 0.0164042 ft]; 銘板_Height=5  [stored 0.0164042 ft]; 銘板_Width=5  [stored 0.0164042 ft]; 銘板表示=いいえ; 電動機出力=750 W; 電圧=415 V

note: [stored X ft] marks values corroborated as IEEE doubles in the binary element streams (Revit-internal decimal feet)
